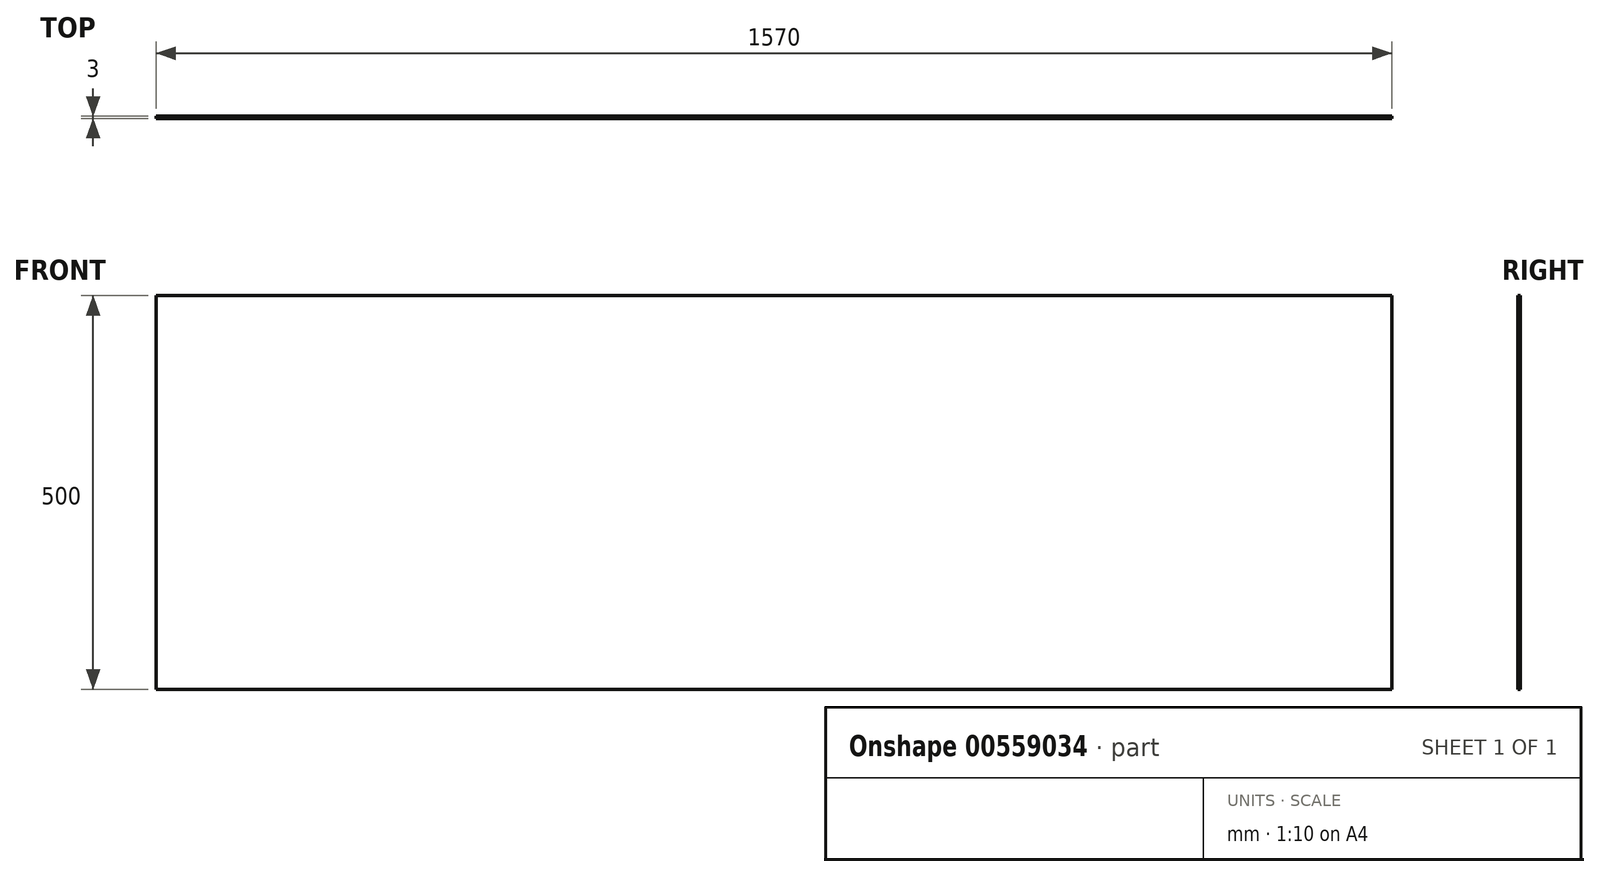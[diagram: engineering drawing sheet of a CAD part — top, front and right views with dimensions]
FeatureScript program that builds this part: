
annotation { "Feature Type Name" : "Feature", "Feature Type Description" : "" }
export const myFeature = defineFeature(function(context is Context, id is Id, definition is map)
    precondition{}
    {
        {
            var Q0;
            Q0=qCreatedBy(makeId("Front.planeOp"),FACE);
            var sketch = newSketch(context, id + "F0", { "sketchPlane" : qUnion([Q0])});
            skLineSegment(sketch, "E0.bottom", {"start": v(0, 0) * mm, "end": v(1570, 0) * mm});
            skLineSegment(sketch, "E0.top", {"start": v(0, 500) * mm, "end": v(1570, 500) * mm});
            skLineSegment(sketch, "E0.left", {"start": v(0, 0) * mm, "end": v(0, 500) * mm});
            skLineSegment(sketch, "E0.right", {"start": v(1570, 0) * mm, "end": v(1570, 500) * mm});
            skSolve(sketch);
        }
        {
            var Q0;
            Q0=makeQuery(id+"F0.imprint","IMPRINT",FACE,{"disambiguationData":[TD([[makeQuery(id+"F0.imprint","IMPRINT",EDGE,{"derivedFrom":sQuery(id+"F0.wireOp",EDGE,"E0.bottom")}),1.0]])]});
            extrude(context, id + "F1", {"entities" : qUnion([Q0]), "depth" : 3 * mm, "offsetDistance" : 25 * mm});
        }
    });
